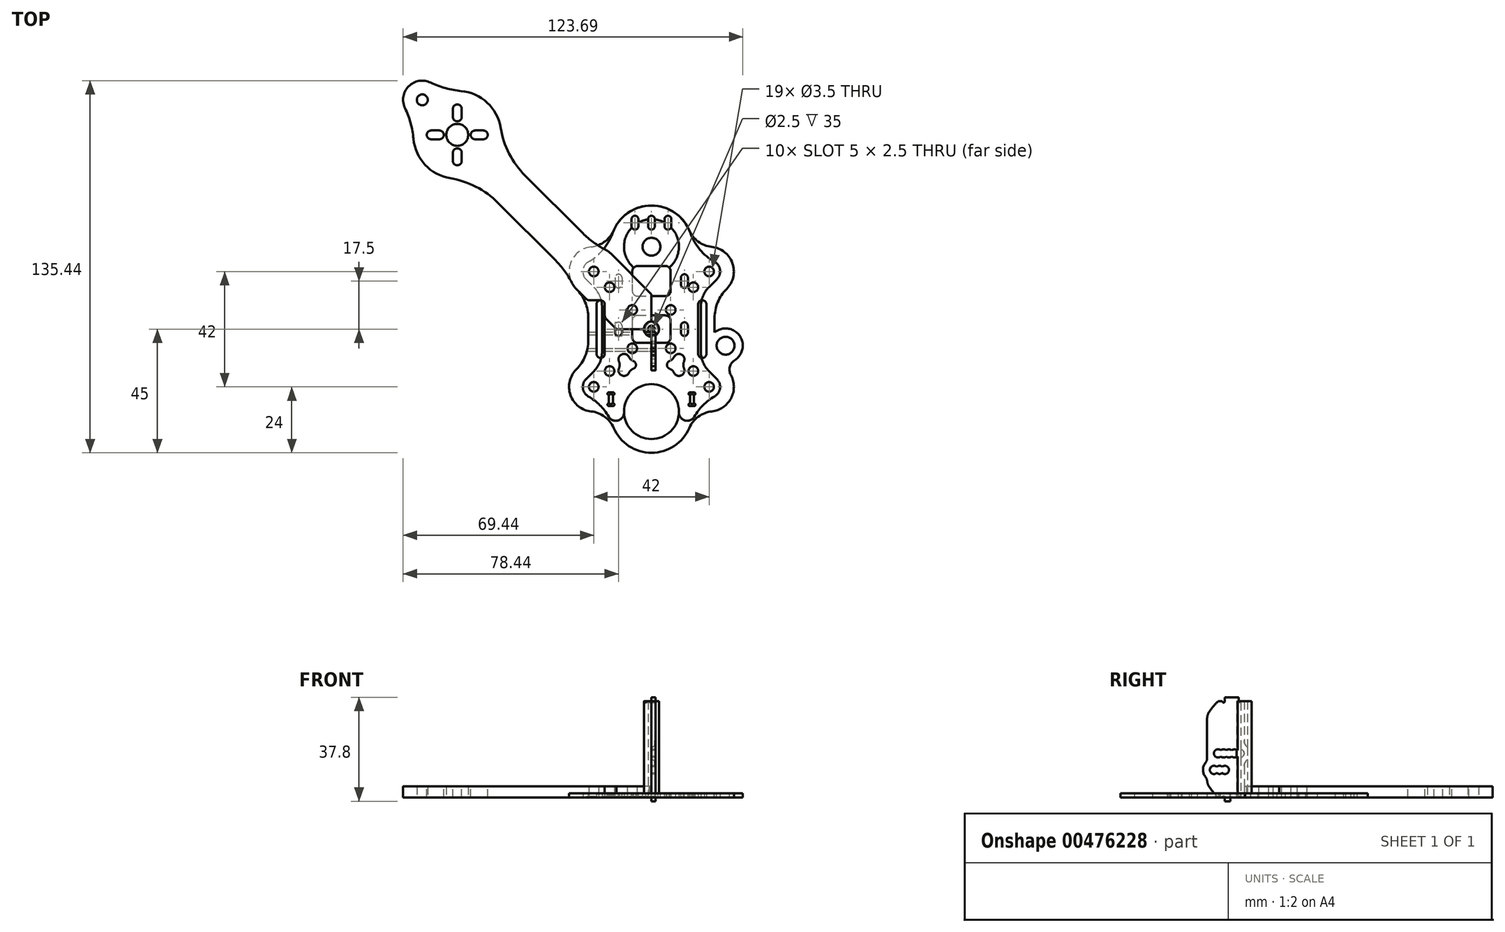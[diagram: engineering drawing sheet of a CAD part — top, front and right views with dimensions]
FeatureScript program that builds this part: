
annotation { "Feature Type Name" : "Feature", "Feature Type Description" : "" }
export const myFeature = defineFeature(function(context is Context, id is Id, definition is map)
    precondition{}
    {
        {
            var Q0;
            Q0=qCreatedBy(makeId("Top.planeOp"),FACE);
            var sketch = newSketch(context, id + "F0", { "sketchPlane" : qUnion([Q0])});
            skCircle(sketch, "E0", {"center": v(-15.25, 15.25) * mm, "radius": 1.75 * mm});
            skCircle(sketch, "E1", {"center": v(15.25, 15.25) * mm, "radius": 1.75 * mm});
            skCircle(sketch, "E2", {"center": v(15.25, -15.25) * mm, "radius": 1.75 * mm});
            skCircle(sketch, "E3", {"center": v(-15.25, -15.25) * mm, "radius": 1.75 * mm});
            skCircle(sketch, "E4", {"center": v(-7, 7) * mm, "radius": 1.75 * mm});
            skCircle(sketch, "E5.MirrorC", {"center": v(7, 7) * mm, "radius": 1.75 * mm});
            skCircle(sketch, "E6.MirrorC", {"center": v(-7, -7) * mm, "radius": 1.75 * mm});
            skCircle(sketch, "E7.MirrorC", {"center": v(7, -7) * mm, "radius": 1.75 * mm});
            skCircle(sketch, "E8", {"center": v(-21, 21) * mm, "radius": 1.75 * mm});
            skCircle(sketch, "E9.MirrorC", {"center": v(21, 21) * mm, "radius": 1.75 * mm});
            skCircle(sketch, "E10.MirrorC", {"center": v(-21, -21) * mm, "radius": 1.75 * mm});
            skCircle(sketch, "E11.MirrorC", {"center": v(21, -21) * mm, "radius": 1.75 * mm});
            skArc(sketch, "E12", {"start": v(-14.64, 27.36) * mm, "mid": v(-27.36, 27.36) * mm, "end": v(-27.36, 14.64) * mm});
            skLineSegment(sketch, "E13", {"start": v(-17, 9) * mm, "end": v(-17, -9.5) * mm});
            skLineSegment(sketch, "E14", {"start": v(-22.6, 10.5) * mm, "end": v(-18.5, 10.5) * mm});
            skLineSegment(sketch, "E15", {"start": v(-22.81, -10.5) * mm, "end": v(-18, -10.5) * mm});
            skLineSegment(sketch, "E16", {"start": v(-14.64, 27.36) * mm, "end": v(-12.37, 25.1) * mm});
            skLineSegment(sketch, "E17", {"start": v(-27.36, 14.64) * mm, "end": v(-23.67, 10.94) * mm});
            skLineSegment(sketch, "E18.MirrorCS", {"start": v(-27.36, -14.64) * mm, "end": v(-23.52, -10.8) * mm});
            skArc(sketch, "E19.MirrorCS", {"start": v(-14.64, -27.36) * mm, "mid": v(-27.36, -27.36) * mm, "end": v(-27.36, -14.64) * mm});
            skLineSegment(sketch, "E20.MirrorCS", {"start": v(-14.64, -27.36) * mm, "end": v(-12.37, -25.1) * mm});
            skLineSegment(sketch, "E21.MirrorCS", {"start": v(14.64, 27.36) * mm, "end": v(12.37, 25.1) * mm});
            skArc(sketch, "E22.MirrorCS", {"start": v(14.64, 27.36) * mm, "mid": v(27.36, 27.36) * mm, "end": v(27.36, 14.64) * mm});
            skLineSegment(sketch, "E23.MirrorCS", {"start": v(27.36, 14.64) * mm, "end": v(23.52, 10.8) * mm});
            skLineSegment(sketch, "E24.MirrorCS", {"start": v(22.81, 10.5) * mm, "end": v(18, 10.5) * mm});
            skLineSegment(sketch, "E25.MirrorCS", {"start": v(17, 9.5) * mm, "end": v(17, -9.5) * mm});
            skLineSegment(sketch, "E26.MirrorCS", {"start": v(22.81, -10.5) * mm, "end": v(18, -10.5) * mm});
            skLineSegment(sketch, "E27.MirrorCS", {"start": v(27.36, -14.64) * mm, "end": v(23.52, -10.8) * mm});
            skArc(sketch, "E28.MirrorCS", {"start": v(14.64, -27.36) * mm, "mid": v(27.36, -27.36) * mm, "end": v(27.36, -14.64) * mm});
            skLineSegment(sketch, "E29.MirrorCS", {"start": v(14.64, -27.36) * mm, "end": v(12.37, -25.1) * mm});
            skPoint(sketch, "E30.visualSharp", {"position": v(0, 12.73) * mm});
            skPoint(sketch, "E31.visualSharp", {"position": v(0, -12.73) * mm});
            skArc(sketch, "E31.filletArc", {"start": v(12.37, -25.1) * mm, "mid": v(0, -19.98) * mm, "end": v(-12.37, -25.1) * mm});
            skPoint(sketch, "E32.visualSharp", {"position": v(-23.23, 10.5) * mm});
            skArc(sketch, "E32.filletArc", {"start": v(-23.67, 10.94) * mm, "mid": v(-23.18, 10.61) * mm, "end": v(-22.6, 10.5) * mm});
            skPoint(sketch, "E33.visualSharp", {"position": v(-17, 10.5) * mm});
            skArc(sketch, "E33.filletArc", {"start": v(-17, 9) * mm, "mid": v(-17.44, 10.06) * mm, "end": v(-18.5, 10.5) * mm});
            skPoint(sketch, "E34.visualSharp", {"position": v(-17, -10.5) * mm});
            skArc(sketch, "E34.filletArc", {"start": v(-18, -10.5) * mm, "mid": v(-17.3, -10.2) * mm, "end": v(-17, -9.5) * mm});
            skPoint(sketch, "E35.visualSharp", {"position": v(-23.23, -10.5) * mm});
            skArc(sketch, "E35.filletArc", {"start": v(-22.81, -10.5) * mm, "mid": v(-23.2, -10.58) * mm, "end": v(-23.52, -10.8) * mm});
            skPoint(sketch, "E36.visualSharp", {"position": v(17, -10.5) * mm});
            skArc(sketch, "E36.filletArc", {"start": v(17, -9.5) * mm, "mid": v(17.3, -10.2) * mm, "end": v(18, -10.5) * mm});
            skPoint(sketch, "E37.visualSharp", {"position": v(23.23, -10.5) * mm});
            skArc(sketch, "E37.filletArc", {"start": v(23.52, -10.8) * mm, "mid": v(23.2, -10.58) * mm, "end": v(22.81, -10.5) * mm});
            skPoint(sketch, "E38.visualSharp", {"position": v(17, 10.5) * mm});
            skArc(sketch, "E38.filletArc", {"start": v(18, 10.5) * mm, "mid": v(17.3, 10.2) * mm, "end": v(17, 9.5) * mm});
            skPoint(sketch, "E39.visualSharp", {"position": v(23.23, 10.5) * mm});
            skArc(sketch, "E39.filletArc", {"start": v(22.81, 10.5) * mm, "mid": v(23.2, 10.58) * mm, "end": v(23.52, 10.8) * mm});
            skLineSegment(sketch, "E40", {"start": v(-21, 21) * mm, "end": v(0, 0) * mm, "construction": true});
            skArc(sketch, "E41.filletArc", {"start": v(-12.37, 25.1) * mm, "mid": v(0, 19.98) * mm, "end": v(12.37, 25.1) * mm});
            skSolve(sketch);
        }
        {
            var Q0;
            Q0=makeQuery(id+"F0.imprint","IMPRINT",FACE,{"disambiguationData":[TD([[makeQuery(id+"F0.imprint","IMPRINT",EDGE,{"derivedFrom":sQuery(id+"F0.wireOp",EDGE,"E0")}),-1.0]])]});
            extrude(context, id + "F1", {"entities" : qUnion([Q0]), "depth" : 1.5 * mm});
        }
        {
            var Q0;
            Q0=qCreatedBy(makeId("Top.planeOp"),FACE);
            var sketch = newSketch(context, id + "F2", { "sketchPlane" : qUnion([Q0])});
            skCircle(sketch, "E42", {"center": v(-15.25, 15.25) * mm, "radius": 1.75 * mm});
            skCircle(sketch, "E43", {"center": v(-7, 7) * mm, "radius": 2.23 * mm});
            skCircle(sketch, "E44", {"center": v(-21, 21) * mm, "radius": 1.75 * mm});
            skArc(sketch, "E45", {"start": v(-21.93, 29.95) * mm, "mid": v(-29.48, 24.01) * mm, "end": v(-27.36, 14.64) * mm});
            skLineSegment(sketch, "E46", {"start": v(-17, 9) * mm, "end": v(-17, 0) * mm});
            skLineSegment(sketch, "E47", {"start": v(-18.5, 10.5) * mm, "end": v(-18.5, 10.5) * mm});
            skLineSegment(sketch, "E48", {"start": v(-20, 9) * mm, "end": v(-20, 0) * mm});
            skPoint(sketch, "E49.visualSharp", {"position": v(-20, 10.5) * mm});
            skArc(sketch, "E49.filletArc", {"start": v(-18.5, 10.5) * mm, "mid": v(-19.56, 10.06) * mm, "end": v(-20, 9) * mm});
            skPoint(sketch, "E50.visualSharp", {"position": v(-17, 10.5) * mm});
            skArc(sketch, "E50.filletArc", {"start": v(-17, 9) * mm, "mid": v(-17.44, 10.06) * mm, "end": v(-18.5, 10.5) * mm});
            skArc(sketch, "E51", {"start": v(0, 45) * mm, "mid": v(-8.24, 42.53) * mm, "end": v(-13.77, 35.94) * mm});
            skArc(sketch, "E52", {"start": v(-21.93, 29.95) * mm, "mid": v(-17.04, 31.84) * mm, "end": v(-13.77, 35.94) * mm});
            skLineSegment(sketch, "E53", {"start": v(0, 45) * mm, "end": v(0, -45) * mm, "construction": true});
            skArc(sketch, "E54", {"start": v(0, 40) * mm, "mid": v(-10, 30) * mm, "end": v(0, 20) * mm});
            skArc(sketch, "E55.MirrorCS", {"start": v(18.5, 10.5) * mm, "mid": v(19.56, 10.06) * mm, "end": v(20, 9) * mm});
            skArc(sketch, "E56.MirrorCS", {"start": v(17, 9) * mm, "mid": v(17.44, 10.06) * mm, "end": v(18.5, 10.5) * mm});
            skLineSegment(sketch, "E57.MirrorCS", {"start": v(18.5, 10.5) * mm, "end": v(18.5, 10.5) * mm});
            skLineSegment(sketch, "E58.MirrorCS", {"start": v(17, 9) * mm, "end": v(17, 0) * mm});
            skArc(sketch, "E59.MirrorCS", {"start": v(21.93, 29.95) * mm, "mid": v(29.48, 24.01) * mm, "end": v(27.36, 14.64) * mm});
            skCircle(sketch, "E60.MirrorC", {"center": v(21, 21) * mm, "radius": 1.75 * mm});
            skCircle(sketch, "E61.MirrorC", {"center": v(7, 7) * mm, "radius": 2.23 * mm});
            skCircle(sketch, "E62.MirrorC", {"center": v(15.25, 15.25) * mm, "radius": 1.75 * mm});
            skArc(sketch, "E63.MirrorCS", {"start": v(21.93, 29.95) * mm, "mid": v(17.04, 31.84) * mm, "end": v(13.77, 35.94) * mm});
            skPoint(sketch, "E64.MirrorP", {"position": v(20, 10.5) * mm});
            skLineSegment(sketch, "E65.MirrorCS", {"start": v(20, 9) * mm, "end": v(20, 0) * mm});
            skPoint(sketch, "E66.MirrorP", {"position": v(17, 10.5) * mm});
            skArc(sketch, "E67.MirrorCS", {"start": v(0, 40) * mm, "mid": v(10, 30) * mm, "end": v(0, 20) * mm});
            skArc(sketch, "E68.MirrorCS", {"start": v(0, 45) * mm, "mid": v(8.24, 42.53) * mm, "end": v(13.77, 35.94) * mm});
            skPoint(sketch, "E69.MirrorP", {"position": v(20, -10.5) * mm});
            skLineSegment(sketch, "E70.MirrorCS", {"start": v(18.5, -10.5) * mm, "end": v(18.5, -10.5) * mm});
            skPoint(sketch, "E71.MirrorP", {"position": v(17, -10.5) * mm});
            skArc(sketch, "E72.MirrorCS", {"start": v(17, -9) * mm, "mid": v(17.44, -10.06) * mm, "end": v(18.5, -10.5) * mm});
            skLineSegment(sketch, "E73.MirrorCS", {"start": v(20, -9) * mm, "end": v(20, 0) * mm});
            skLineSegment(sketch, "E74.MirrorCS", {"start": v(17, -9) * mm, "end": v(17, 0) * mm});
            skArc(sketch, "E75.MirrorCS", {"start": v(18.5, -10.5) * mm, "mid": v(19.56, -10.06) * mm, "end": v(20, -9) * mm});
            skArc(sketch, "E76.MirrorCS", {"start": v(-17, -9) * mm, "mid": v(-17.44, -10.06) * mm, "end": v(-18.5, -10.5) * mm});
            skArc(sketch, "E77.MirrorCS", {"start": v(-18.5, -10.5) * mm, "mid": v(-19.56, -10.06) * mm, "end": v(-20, -9) * mm});
            skLineSegment(sketch, "E78.MirrorCS", {"start": v(-20, -9) * mm, "end": v(-20, 0) * mm});
            skLineSegment(sketch, "E79.MirrorCS", {"start": v(-17, -9) * mm, "end": v(-17, 0) * mm});
            skPoint(sketch, "E80.MirrorP", {"position": v(-20, -10.5) * mm});
            skPoint(sketch, "E81.MirrorP", {"position": v(-17, -10.5) * mm});
            skLineSegment(sketch, "E82.MirrorCS", {"start": v(-18.5, -10.5) * mm, "end": v(-18.5, -10.5) * mm});
            skCircle(sketch, "E83.MirrorC", {"center": v(-15.25, -15.25) * mm, "radius": 1.75 * mm});
            skCircle(sketch, "E84.MirrorC", {"center": v(-21, -21) * mm, "radius": 1.75 * mm});
            skArc(sketch, "E85.MirrorCS", {"start": v(-21.93, -29.95) * mm, "mid": v(-29.48, -24.01) * mm, "end": v(-27.36, -14.64) * mm});
            skCircle(sketch, "E86.MirrorC", {"center": v(21, -21) * mm, "radius": 1.75 * mm});
            skCircle(sketch, "E87.MirrorC", {"center": v(15.25, -15.25) * mm, "radius": 1.75 * mm});
            skCircle(sketch, "E88.MirrorC", {"center": v(7, -7) * mm, "radius": 2.23 * mm});
            skCircle(sketch, "E89.MirrorC", {"center": v(-7, -7) * mm, "radius": 2.23 * mm});
            skArc(sketch, "E90.MirrorCS", {"start": v(21.93, -29.95) * mm, "mid": v(29.48, -24.01) * mm, "end": v(27.36, -14.64) * mm});
            skArc(sketch, "E91.MirrorCS", {"start": v(21.93, -29.95) * mm, "mid": v(17.04, -31.84) * mm, "end": v(13.77, -35.94) * mm});
            skArc(sketch, "E92.MirrorCS", {"start": v(0, -45) * mm, "mid": v(8.24, -42.53) * mm, "end": v(13.77, -35.94) * mm});
            skArc(sketch, "E93.MirrorCS", {"start": v(0, -45) * mm, "mid": v(-8.24, -42.53) * mm, "end": v(-13.77, -35.94) * mm});
            skArc(sketch, "E94.MirrorCS", {"start": v(-21.93, -29.95) * mm, "mid": v(-17.04, -31.84) * mm, "end": v(-13.77, -35.94) * mm});
            skArc(sketch, "E95.MirrorCS", {"start": v(0, -40) * mm, "mid": v(-10, -30) * mm, "end": v(0, -20) * mm});
            skArc(sketch, "E96.MirrorCS", {"start": v(0, -40) * mm, "mid": v(10, -30) * mm, "end": v(0, -20) * mm});
            skLineSegment(sketch, "E97.bottom", {"start": v(-15.5, -23) * mm, "end": v(-14, -23) * mm});
            skLineSegment(sketch, "E97.top", {"start": v(-15.5, -28) * mm, "end": v(-14, -28) * mm});
            skLineSegment(sketch, "E97.left", {"start": v(-15.5, -23) * mm, "end": v(-15.5, -28) * mm});
            skLineSegment(sketch, "E97.right", {"start": v(-14, -23) * mm, "end": v(-14, -28) * mm});
            skLineSegment(sketch, "E98.MirrorCS", {"start": v(15.5, -23) * mm, "end": v(14, -23) * mm});
            skLineSegment(sketch, "E99.MirrorCS", {"start": v(15.5, -23) * mm, "end": v(15.5, -28) * mm});
            skLineSegment(sketch, "E100.MirrorCS", {"start": v(14, -23) * mm, "end": v(14, -28) * mm});
            skLineSegment(sketch, "E101.MirrorCS", {"start": v(15.5, -28) * mm, "end": v(14, -28) * mm});
            skLineSegment(sketch, "E102", {"start": v(-27.36, -14.64) * mm, "end": v(-27.36, -14.64) * mm});
            skLineSegment(sketch, "E103", {"start": v(-21, -21) * mm, "end": v(0, 0) * mm, "construction": true});
            skLineSegment(sketch, "E104", {"start": v(-22.97, -4.03) * mm, "end": v(-22.97, 0) * mm});
            skPoint(sketch, "E105.visualSharp", {"position": v(-22.97, -10.24) * mm});
            skArc(sketch, "E105.filletArc", {"start": v(-27.36, -14.64) * mm, "mid": v(-24.11, -9.77) * mm, "end": v(-22.97, -4.03) * mm});
            skArc(sketch, "E106.MirrorCS", {"start": v(27.36, -14.64) * mm, "mid": v(24.11, -9.77) * mm, "end": v(22.97, -4.03) * mm});
            skLineSegment(sketch, "E107.MirrorCS", {"start": v(22.97, -4.03) * mm, "end": v(22.97, 0) * mm});
            skArc(sketch, "E108.MirrorCS", {"start": v(27.36, 14.64) * mm, "mid": v(24.11, 9.77) * mm, "end": v(22.97, 4.03) * mm});
            skLineSegment(sketch, "E109.MirrorCS", {"start": v(22.97, 4.03) * mm, "end": v(22.97, 0) * mm});
            skLineSegment(sketch, "E110.MirrorCS", {"start": v(-22.97, 4.03) * mm, "end": v(-22.97, 0) * mm});
            skArc(sketch, "E111.MirrorCS", {"start": v(-27.36, 14.64) * mm, "mid": v(-24.11, 9.77) * mm, "end": v(-22.97, 4.03) * mm});
            skSolve(sketch);
        }
        {
            var Q0;
            Q0=makeQuery(id+"F2.imprint","IMPRINT",FACE,{"disambiguationData":[TD([[makeQuery(id+"F2.imprint","IMPRINT",EDGE,{"derivedFrom":sQuery(id+"F2.wireOp",EDGE,"E42")}),-1.0]])]});
            extrude(context, id + "F3", {"entities" : qUnion([Q0]), "depth" : 1.5 * mm});
        }
        {
            var Q0;
            Q0=makeQuery(id+"F3.opExtrude","CAP_FACE",FACE,{"disambiguationData":[OSD([sQuery(id+"F2.wireOp",EDGE,"E42"),sQuery(id+"F2.wireOp",EDGE,"E43"),sQuery(id+"F2.wireOp",EDGE,"E44"),sQuery(id+"F2.wireOp",EDGE,"E45"),sQuery(id+"F2.wireOp",EDGE,"E46"),sQuery(id+"F2.wireOp",EDGE,"E48"),sQuery(id+"F2.wireOp",EDGE,"E49.filletArc"),sQuery(id+"F2.wireOp",EDGE,"E50.filletArc"),sQuery(id+"F2.wireOp",EDGE,"E51"),sQuery(id+"F2.wireOp",EDGE,"E52"),sQuery(id+"F2.wireOp",EDGE,"E54"),sQuery(id+"F2.wireOp",EDGE,"E55.MirrorCS"),sQuery(id+"F2.wireOp",EDGE,"E56.MirrorCS"),sQuery(id+"F2.wireOp",EDGE,"E58.MirrorCS"),sQuery(id+"F2.wireOp",EDGE,"E59.MirrorCS"),sQuery(id+"F2.wireOp",EDGE,"E60.MirrorC"),sQuery(id+"F2.wireOp",EDGE,"E61.MirrorC"),sQuery(id+"F2.wireOp",EDGE,"E62.MirrorC"),sQuery(id+"F2.wireOp",EDGE,"E63.MirrorCS"),sQuery(id+"F2.wireOp",EDGE,"E65.MirrorCS"),sQuery(id+"F2.wireOp",EDGE,"E67.MirrorCS"),sQuery(id+"F2.wireOp",EDGE,"E68.MirrorCS"),sQuery(id+"F2.wireOp",EDGE,"E72.MirrorCS"),sQuery(id+"F2.wireOp",EDGE,"E73.MirrorCS"),sQuery(id+"F2.wireOp",EDGE,"E74.MirrorCS"),sQuery(id+"F2.wireOp",EDGE,"E75.MirrorCS"),sQuery(id+"F2.wireOp",EDGE,"E76.MirrorCS"),sQuery(id+"F2.wireOp",EDGE,"E77.MirrorCS"),sQuery(id+"F2.wireOp",EDGE,"E78.MirrorCS"),sQuery(id+"F2.wireOp",EDGE,"E79.MirrorCS"),sQuery(id+"F2.wireOp",EDGE,"E83.MirrorC"),sQuery(id+"F2.wireOp",EDGE,"E84.MirrorC"),sQuery(id+"F2.wireOp",EDGE,"E85.MirrorCS"),sQuery(id+"F2.wireOp",EDGE,"E86.MirrorC"),sQuery(id+"F2.wireOp",EDGE,"E87.MirrorC"),sQuery(id+"F2.wireOp",EDGE,"E88.MirrorC"),sQuery(id+"F2.wireOp",EDGE,"E89.MirrorC"),sQuery(id+"F2.wireOp",EDGE,"E90.MirrorCS"),sQuery(id+"F2.wireOp",EDGE,"E91.MirrorCS"),sQuery(id+"F2.wireOp",EDGE,"E92.MirrorCS"),sQuery(id+"F2.wireOp",EDGE,"E93.MirrorCS"),sQuery(id+"F2.wireOp",EDGE,"E94.MirrorCS"),sQuery(id+"F2.wireOp",EDGE,"E95.MirrorCS"),sQuery(id+"F2.wireOp",EDGE,"E96.MirrorCS"),sQuery(id+"F2.wireOp",EDGE,"E97.bottom"),sQuery(id+"F2.wireOp",EDGE,"E97.top"),sQuery(id+"F2.wireOp",EDGE,"E97.left"),sQuery(id+"F2.wireOp",EDGE,"E97.right"),sQuery(id+"F2.wireOp",EDGE,"E98.MirrorCS"),sQuery(id+"F2.wireOp",EDGE,"E99.MirrorCS"),sQuery(id+"F2.wireOp",EDGE,"E100.MirrorCS"),sQuery(id+"F2.wireOp",EDGE,"E101.MirrorCS"),sQuery(id+"F2.wireOp",EDGE,"E104"),sQuery(id+"F2.wireOp",EDGE,"E105.filletArc"),sQuery(id+"F2.wireOp",EDGE,"E106.MirrorCS"),sQuery(id+"F2.wireOp",EDGE,"E107.MirrorCS"),sQuery(id+"F2.wireOp",EDGE,"E108.MirrorCS"),sQuery(id+"F2.wireOp",EDGE,"E109.MirrorCS"),sQuery(id+"F2.wireOp",EDGE,"E110.MirrorCS"),sQuery(id+"F2.wireOp",EDGE,"E111.MirrorCS")])],"isStart":true});
            var sketch = newSketch(context, id + "F4", { "sketchPlane" : qUnion([Q0])});
            skCircle(sketch, "E112", {"center": v(-15.5, 27.5) * mm, "radius": 0.5 * mm});
            skCircle(sketch, "E113", {"center": v(-14, 27.5) * mm, "radius": 0.5 * mm});
            skCircle(sketch, "E114", {"center": v(-15.5, 23.5) * mm, "radius": 0.5 * mm});
            skCircle(sketch, "E115", {"center": v(-14, 23.5) * mm, "radius": 0.5 * mm});
            skCircle(sketch, "E116.MirrorC", {"center": v(14, 23.5) * mm, "radius": 0.5 * mm});
            skCircle(sketch, "E117.MirrorC", {"center": v(15.5, 27.5) * mm, "radius": 0.5 * mm});
            skCircle(sketch, "E118.MirrorC", {"center": v(14, 27.5) * mm, "radius": 0.5 * mm});
            skCircle(sketch, "E119.MirrorC", {"center": v(15.5, 23.5) * mm, "radius": 0.5 * mm});
            skSolve(sketch);
        }
        {
            var Q0;
            Q0 = qSketchRegion(id + "F4", true);
            extrude(context, id + "F5", {"entities" : qUnion([Q0]), "operationType" : NewBodyOperationType.REMOVE, "oppositeDirection" : true, "depth" : 25 * mm});
        }
        {
            var Q0;
            Q0=qCreatedBy(makeId("Top.planeOp"),FACE);
            var sketch = newSketch(context, id + "F6", { "sketchPlane" : qUnion([Q0])});
            skCircle(sketch, "E120", {"center": v(-7, 7) * mm, "radius": 1.75 * mm});
            skCircle(sketch, "E121", {"center": v(-15.25, 15.25) * mm, "radius": 1.75 * mm});
            skCircle(sketch, "E122", {"center": v(-21, 21) * mm, "radius": 1.75 * mm});
            skArc(sketch, "E123", {"start": v(-17, 9) * mm, "mid": v(-17.44, 10.06) * mm, "end": v(-18.5, 10.5) * mm});
            skLineSegment(sketch, "E124", {"start": v(0, 0) * mm, "end": v(-70.71, 70.71) * mm, "construction": true});
            skLineSegment(sketch, "E125", {"start": v(0, 12.73) * mm, "end": v(-14.64, 27.36) * mm});
            skLineSegment(sketch, "E126", {"start": v(-12.73, 0) * mm, "end": v(-16.56, 3.83) * mm});
            skLineSegment(sketch, "E127", {"start": v(-17, 9) * mm, "end": v(-17, 4.9) * mm});
            skLineSegment(sketch, "E128", {"start": v(-18.5, 10.5) * mm, "end": v(-22.6, 10.5) * mm});
            skLineSegment(sketch, "E129.trimOffspring", {"start": v(-23.67, 10.94) * mm, "end": v(-27.36, 14.64) * mm});
            skLineSegment(sketch, "E130", {"start": v(-12.73, 0) * mm, "end": v(0, 0) * mm});
            skLineSegment(sketch, "E131", {"start": v(0, 0) * mm, "end": v(0, 12.73) * mm});
            skPoint(sketch, "E132.visualSharp", {"position": v(-23.23, 10.5) * mm});
            skArc(sketch, "E132.filletArc", {"start": v(-23.67, 10.94) * mm, "mid": v(-23.18, 10.61) * mm, "end": v(-22.6, 10.5) * mm});
            skPoint(sketch, "E133.visualSharp", {"position": v(-17, 4.27) * mm});
            skArc(sketch, "E133.filletArc", {"start": v(-17, 4.9) * mm, "mid": v(-16.89, 4.32) * mm, "end": v(-16.56, 3.83) * mm});
            skArc(sketch, "E134", {"start": v(-86.65, 69.27) * mm, "mid": v(-82.43, 59.82) * mm, "end": v(-73.3, 54.92) * mm});
            skArc(sketch, "E135", {"start": v(-80.38, 89.73) * mm, "mid": v(-88.39, 88.39) * mm, "end": v(-89.73, 80.38) * mm});
            skCircle(sketch, "E136", {"center": v(-83.44, 83.44) * mm, "radius": 2 * mm});
            skLineSegment(sketch, "E137", {"start": v(-70.71, 70.71) * mm, "end": v(-83.44, 83.44) * mm, "construction": true});
            skPoint(sketch, "E138.visualSharp", {"position": v(-76.76, 85.52) * mm});
            skArc(sketch, "E138.filletArc", {"start": v(-80.38, 89.73) * mm, "mid": v(-74.97, 87.69) * mm, "end": v(-69.27, 86.65) * mm});
            skPoint(sketch, "E139.visualSharp", {"position": v(-85.52, 76.76) * mm});
            skArc(sketch, "E139.filletArc", {"start": v(-86.65, 69.27) * mm, "mid": v(-87.69, 74.97) * mm, "end": v(-89.73, 80.38) * mm});
            skCircle(sketch, "E140", {"center": v(-70.71, 70.71) * mm, "radius": 64.25 * mm, "construction": true});
            skArc(sketch, "E141.trimOffspring", {"start": v(-54.92, 73.3) * mm, "mid": v(-59.82, 82.43) * mm, "end": v(-69.27, 86.65) * mm});
            skCircle(sketch, "E142", {"center": v(-70.71, 70.71) * mm, "radius": 4 * mm});
            skArc(sketch, "E143.trimOffspring", {"start": v(-14.64, 27.36) * mm, "mid": v(-15.7, 28.28) * mm, "end": v(-16.9, 29.02) * mm});
            skLineSegment(sketch, "E144", {"start": v(-45.97, 55.87) * mm, "end": v(-25, 34.9) * mm});
            skLineSegment(sketch, "E145", {"start": v(-55.87, 45.97) * mm, "end": v(-34.9, 25) * mm});
            skPoint(sketch, "E146.visualSharp", {"position": v(-65.49, 55.59) * mm});
            skArc(sketch, "E146.filletArc", {"start": v(-55.87, 45.97) * mm, "mid": v(-63.89, 51.82) * mm, "end": v(-73.3, 54.92) * mm});
            skPoint(sketch, "E147.visualSharp", {"position": v(-55.59, 65.49) * mm});
            skArc(sketch, "E147.filletArc", {"start": v(-54.92, 73.3) * mm, "mid": v(-51.82, 63.89) * mm, "end": v(-45.97, 55.87) * mm});
            skArc(sketch, "E148.trimOffspring", {"start": v(-29.02, 16.9) * mm, "mid": v(-28.28, 15.7) * mm, "end": v(-27.36, 14.64) * mm});
            skPoint(sketch, "E149.visualSharp", {"position": v(-20.05, 29.95) * mm});
            skArc(sketch, "E149.filletArc", {"start": v(-25, 34.9) * mm, "mid": v(-21.18, 31.64) * mm, "end": v(-16.9, 29.02) * mm});
            skPoint(sketch, "E150.visualSharp", {"position": v(-29.95, 20.05) * mm});
            skArc(sketch, "E150.filletArc", {"start": v(-29.02, 16.9) * mm, "mid": v(-31.64, 21.18) * mm, "end": v(-34.9, 25) * mm});
            skSolve(sketch);
        }
        {
            var Q0;
            Q0=makeQuery(id+"F6.imprint","IMPRINT",FACE,{"disambiguationData":[TD([[makeQuery(id+"F6.imprint","IMPRINT",EDGE,{"derivedFrom":sQuery(id+"F6.wireOp",EDGE,"E120")}),-1.0]])]});
            extrude(context, id + "F7", {"entities" : qUnion([Q0]), "depth" : 4 * mm});
        }
        {
            var Q0;
            Q0=makeQuery(id+"F7.opExtrude","CAP_FACE",FACE,{"disambiguationData":[OSD([sQuery(id+"F6.wireOp",EDGE,"E120"),sQuery(id+"F6.wireOp",EDGE,"E121"),sQuery(id+"F6.wireOp",EDGE,"E122"),sQuery(id+"F6.wireOp",EDGE,"E123"),sQuery(id+"F6.wireOp",EDGE,"E125"),sQuery(id+"F6.wireOp",EDGE,"E126"),sQuery(id+"F6.wireOp",EDGE,"E127"),sQuery(id+"F6.wireOp",EDGE,"E128"),sQuery(id+"F6.wireOp",EDGE,"E129.trimOffspring"),sQuery(id+"F6.wireOp",EDGE,"E130"),sQuery(id+"F6.wireOp",EDGE,"E131"),sQuery(id+"F6.wireOp",EDGE,"E132.filletArc"),sQuery(id+"F6.wireOp",EDGE,"E133.filletArc"),sQuery(id+"F6.wireOp",EDGE,"E134"),sQuery(id+"F6.wireOp",EDGE,"E135"),sQuery(id+"F6.wireOp",EDGE,"E136"),sQuery(id+"F6.wireOp",EDGE,"E138.filletArc"),sQuery(id+"F6.wireOp",EDGE,"E139.filletArc"),sQuery(id+"F6.wireOp",EDGE,"E141.trimOffspring"),sQuery(id+"F6.wireOp",EDGE,"7c681801-0f79-4b64-9db9-c0788a7385f7.filletArc"),sQuery(id+"F6.wireOp",EDGE,"abeb74fd-95f9-49b4-a37d-9e8ca5098ea8.filletArc"),sQuery(id+"F6.wireOp",EDGE,"E142")])],"isStart":false});
            var sketch = newSketch(context, id + "F8", { "sketchPlane" : qUnion([Q0])});
            skLineSegment(sketch, "E151", {"start": v(-70.71, 70.71) * mm, "end": v(-64.21, 70.71) * mm, "construction": true});
            skLineSegment(sketch, "E152", {"start": v(-70.71, 70.71) * mm, "end": v(0, 0) * mm, "construction": true});
            skLineSegment(sketch, "E153", {"start": v(-64.21, 70.71) * mm, "end": v(-61.21, 70.71) * mm, "construction": true});
            skArc(sketch, "E154.0.startCap", {"start": v(-64.21, 69.11) * mm, "mid": v(-65.81, 70.71) * mm, "end": v(-64.21, 72.31) * mm});
            skArc(sketch, "E154.0.endCap", {"start": v(-61.21, 72.31) * mm, "mid": v(-59.61, 70.71) * mm, "end": v(-61.21, 69.11) * mm});
            skLineSegment(sketch, "E154.0.left", {"start": v(-64.21, 72.31) * mm, "end": v(-61.21, 72.31) * mm});
            skLineSegment(sketch, "E154.0.right", {"start": v(-64.21, 69.11) * mm, "end": v(-61.21, 69.11) * mm});
            skLineSegment(sketch, "E155.1.0", {"start": v(-72.31, 77.21) * mm, "end": v(-72.31, 80.21) * mm});
            skArc(sketch, "E155.1.1", {"start": v(-69.11, 77.21) * mm, "mid": v(-70.71, 75.61) * mm, "end": v(-72.31, 77.21) * mm});
            skLineSegment(sketch, "E155.1.2", {"start": v(-69.11, 77.21) * mm, "end": v(-69.11, 80.21) * mm});
            skArc(sketch, "E155.1.3", {"start": v(-72.31, 80.21) * mm, "mid": v(-70.71, 81.81) * mm, "end": v(-69.11, 80.21) * mm});
            skLineSegment(sketch, "E155.2.0", {"start": v(-77.21, 69.11) * mm, "end": v(-80.21, 69.11) * mm});
            skArc(sketch, "E155.2.1", {"start": v(-77.21, 72.31) * mm, "mid": v(-75.61, 70.71) * mm, "end": v(-77.21, 69.11) * mm});
            skLineSegment(sketch, "E155.2.2", {"start": v(-77.21, 72.31) * mm, "end": v(-80.21, 72.31) * mm});
            skArc(sketch, "E155.2.3", {"start": v(-80.21, 69.11) * mm, "mid": v(-81.81, 70.71) * mm, "end": v(-80.21, 72.31) * mm});
            skLineSegment(sketch, "E155.3.0", {"start": v(-69.11, 64.21) * mm, "end": v(-69.11, 61.21) * mm});
            skArc(sketch, "E155.3.1", {"start": v(-72.31, 64.21) * mm, "mid": v(-70.71, 65.81) * mm, "end": v(-69.11, 64.21) * mm});
            skLineSegment(sketch, "E155.3.2", {"start": v(-72.31, 64.21) * mm, "end": v(-72.31, 61.21) * mm});
            skArc(sketch, "E155.3.3", {"start": v(-69.11, 61.21) * mm, "mid": v(-70.71, 59.61) * mm, "end": v(-72.31, 61.21) * mm});
            skPoint(sketch, "E155.center", {"position": v(-70.71, 70.71) * mm});
            skSolve(sketch);
        }
        {
            var Q0;
            Q0 = qSketchRegion(id + "F8", true);
            extrude(context, id + "F9", {"entities" : qUnion([Q0]), "operationType" : NewBodyOperationType.REMOVE, "oppositeDirection" : true, "depth" : 25 * mm});
        }
        {
            var Q0;
            Q0=qCreatedBy(makeId("Top.planeOp"),FACE);
            var sketch = newSketch(context, id + "F10", { "sketchPlane" : qUnion([Q0])});
            skCircle(sketch, "E156", {"center": v(-21, 21) * mm, "radius": 1.75 * mm});
            skArc(sketch, "E157", {"start": v(-23, 24.47) * mm, "mid": v(-24.97, 21.53) * mm, "end": v(-23.83, 18.17) * mm});
            skArc(sketch, "E158", {"start": v(0, 45) * mm, "mid": v(-8.63, 42.27) * mm, "end": v(-14.12, 35.06) * mm});
            skArc(sketch, "E159", {"start": v(-23, 24.47) * mm, "mid": v(-17.61, 28.98) * mm, "end": v(-14.12, 35.06) * mm});
            skLineSegment(sketch, "E160", {"start": v(-23.83, 18.17) * mm, "end": v(-20.93, 15.27) * mm});
            skLineSegment(sketch, "E161", {"start": v(-21, 21) * mm, "end": v(0, 0) * mm, "construction": true});
            skLineSegment(sketch, "E162", {"start": v(-18, 8.2) * mm, "end": v(-18, 0) * mm});
            skPoint(sketch, "E163.visualSharp", {"position": v(-18, 12.34) * mm});
            skArc(sketch, "E163.filletArc", {"start": v(-18, 8.2) * mm, "mid": v(-18.76, 12.03) * mm, "end": v(-20.93, 15.27) * mm});
            skLineSegment(sketch, "E164", {"start": v(0, 0) * mm, "end": v(0, 0) * mm});
            skLineSegment(sketch, "E165.MirrorCS", {"start": v(18, 8.2) * mm, "end": v(18, 0) * mm});
            skPoint(sketch, "E166.MirrorP", {"position": v(18, 12.34) * mm});
            skArc(sketch, "E167.MirrorCS", {"start": v(23, 24.47) * mm, "mid": v(17.61, 28.98) * mm, "end": v(14.12, 35.06) * mm});
            skLineSegment(sketch, "E168.MirrorCS", {"start": v(23.83, 18.17) * mm, "end": v(20.93, 15.27) * mm});
            skArc(sketch, "E169.MirrorCS", {"start": v(23, 24.47) * mm, "mid": v(24.97, 21.53) * mm, "end": v(23.83, 18.17) * mm});
            skCircle(sketch, "E170.MirrorC", {"center": v(21, 21) * mm, "radius": 1.75 * mm});
            skArc(sketch, "E171.MirrorCS", {"start": v(0, 45) * mm, "mid": v(8.63, 42.27) * mm, "end": v(14.12, 35.06) * mm});
            skLineSegment(sketch, "E172.MirrorCS", {"start": v(21, 21) * mm, "end": v(0, 0) * mm, "construction": true});
            skArc(sketch, "E173.MirrorCS", {"start": v(18, 8.2) * mm, "mid": v(18.76, 12.03) * mm, "end": v(20.93, 15.27) * mm});
            skLineSegment(sketch, "E174.MirrorCS", {"start": v(0, 45) * mm, "end": v(0, 0) * mm, "construction": true});
            skArc(sketch, "E175.MirrorCS", {"start": v(-18, -8.2) * mm, "mid": v(-18.76, -12.03) * mm, "end": v(-20.93, -15.27) * mm});
            skLineSegment(sketch, "E176.MirrorCS", {"start": v(-18, -8.2) * mm, "end": v(-18, 0) * mm});
            skLineSegment(sketch, "E177.MirrorCS", {"start": v(18, -8.2) * mm, "end": v(18, 0) * mm});
            skArc(sketch, "E178.MirrorCS", {"start": v(18, -8.2) * mm, "mid": v(18.76, -12.03) * mm, "end": v(20.93, -15.27) * mm});
            skLineSegment(sketch, "E179.MirrorCS", {"start": v(23.83, -18.17) * mm, "end": v(20.93, -15.27) * mm});
            skLineSegment(sketch, "E180.MirrorCS", {"start": v(-23.83, -18.17) * mm, "end": v(-20.93, -15.27) * mm});
            skArc(sketch, "E181.MirrorCS", {"start": v(-23, -24.47) * mm, "mid": v(-24.97, -21.53) * mm, "end": v(-23.83, -18.17) * mm});
            skArc(sketch, "E182.MirrorCS", {"start": v(23, -24.47) * mm, "mid": v(24.97, -21.53) * mm, "end": v(23.83, -18.17) * mm});
            skArc(sketch, "E183.MirrorCS", {"start": v(23, -24.47) * mm, "mid": v(18.8, -27.67) * mm, "end": v(15.6, -31.86) * mm});
            skArc(sketch, "E184.MirrorCS", {"start": v(-23, -24.47) * mm, "mid": v(-18.8, -27.67) * mm, "end": v(-15.6, -31.86) * mm});
            skCircle(sketch, "E185.MirrorC", {"center": v(-21, -21) * mm, "radius": 1.75 * mm});
            skCircle(sketch, "E186.MirrorC", {"center": v(21, -21) * mm, "radius": 1.75 * mm});
            skArc(sketch, "E187", {"start": v(10, -30) * mm, "mid": v(0, -20) * mm, "end": v(-10, -30) * mm});
            skLineSegment(sketch, "E188", {"start": v(-10, -30) * mm, "end": v(-10, -30.36) * mm});
            skLineSegment(sketch, "E189.MirrorCS", {"start": v(10, -30) * mm, "end": v(10, -30.36) * mm});
            skPoint(sketch, "E190.orphan", {"position": v(0, -45) * mm});
            skArc(sketch, "E191", {"start": v(-15.6, -31.86) * mm, "mid": v(-12.23, -33.26) * mm, "end": v(-10, -30.36) * mm});
            skPoint(sketch, "E192.orphan", {"position": v(-14.12, -35.06) * mm});
            skArc(sketch, "E193.MirrorCS", {"start": v(15.6, -31.86) * mm, "mid": v(12.23, -33.26) * mm, "end": v(10, -30.36) * mm});
            skPoint(sketch, "E194.orphan", {"position": v(14.12, -35.06) * mm});
            skLineSegment(sketch, "E195.bottom", {"start": v(-15.5, -23) * mm, "end": v(-14, -23) * mm});
            skLineSegment(sketch, "E195.top", {"start": v(-15.5, -28) * mm, "end": v(-14, -28) * mm});
            skLineSegment(sketch, "E195.left", {"start": v(-15.5, -23) * mm, "end": v(-15.5, -28) * mm});
            skLineSegment(sketch, "E195.right", {"start": v(-14, -23) * mm, "end": v(-14, -28) * mm});
            skLineSegment(sketch, "E196.MirrorCS", {"start": v(15.5, -28) * mm, "end": v(14, -28) * mm});
            skLineSegment(sketch, "E197.MirrorCS", {"start": v(14, -23) * mm, "end": v(14, -28) * mm});
            skLineSegment(sketch, "E198.MirrorCS", {"start": v(15.5, -23) * mm, "end": v(15.5, -28) * mm});
            skLineSegment(sketch, "E199.MirrorCS", {"start": v(15.5, -23) * mm, "end": v(14, -23) * mm});
            skSolve(sketch);
        }
        {
            var Q0;
            Q0=makeQuery(id+"F10.imprint","IMPRINT",FACE,{"disambiguationData":[TD([[makeQuery(id+"F10.imprint","IMPRINT",EDGE,{"derivedFrom":sQuery(id+"F10.wireOp",EDGE,"E156")}),-1.0]])]});
            extrude(context, id + "F11", {"entities" : qUnion([Q0]), "depth" : 1.5 * mm});
        }
        {
            var Q0;
            Q0=makeQuery(id+"F11.opExtrude","CAP_FACE",FACE,{"disambiguationData":[OSD([sQuery(id+"F10.wireOp",EDGE,"E156"),sQuery(id+"F10.wireOp",EDGE,"E157"),sQuery(id+"F10.wireOp",EDGE,"E158"),sQuery(id+"F10.wireOp",EDGE,"E159"),sQuery(id+"F10.wireOp",EDGE,"E160"),sQuery(id+"F10.wireOp",EDGE,"E162"),sQuery(id+"F10.wireOp",EDGE,"E163.filletArc"),sQuery(id+"F10.wireOp",EDGE,"E165.MirrorCS"),sQuery(id+"F10.wireOp",EDGE,"E167.MirrorCS"),sQuery(id+"F10.wireOp",EDGE,"E168.MirrorCS"),sQuery(id+"F10.wireOp",EDGE,"E169.MirrorCS"),sQuery(id+"F10.wireOp",EDGE,"E170.MirrorC"),sQuery(id+"F10.wireOp",EDGE,"E171.MirrorCS"),sQuery(id+"F10.wireOp",EDGE,"E173.MirrorCS"),sQuery(id+"F10.wireOp",EDGE,"E175.MirrorCS"),sQuery(id+"F10.wireOp",EDGE,"E176.MirrorCS"),sQuery(id+"F10.wireOp",EDGE,"E177.MirrorCS"),sQuery(id+"F10.wireOp",EDGE,"E178.MirrorCS"),sQuery(id+"F10.wireOp",EDGE,"E179.MirrorCS"),sQuery(id+"F10.wireOp",EDGE,"E180.MirrorCS"),sQuery(id+"F10.wireOp",EDGE,"E181.MirrorCS"),sQuery(id+"F10.wireOp",EDGE,"E182.MirrorCS"),sQuery(id+"F10.wireOp",EDGE,"E183.MirrorCS"),sQuery(id+"F10.wireOp",EDGE,"E184.MirrorCS"),sQuery(id+"F10.wireOp",EDGE,"E185.MirrorC"),sQuery(id+"F10.wireOp",EDGE,"E186.MirrorC"),sQuery(id+"F10.wireOp",EDGE,"E187"),sQuery(id+"F10.wireOp",EDGE,"E188"),sQuery(id+"F10.wireOp",EDGE,"E189.MirrorCS"),sQuery(id+"F10.wireOp",EDGE,"E191"),sQuery(id+"F10.wireOp",EDGE,"E193.MirrorCS"),sQuery(id+"F10.wireOp",EDGE,"E195.bottom"),sQuery(id+"F10.wireOp",EDGE,"E195.top"),sQuery(id+"F10.wireOp",EDGE,"E195.left"),sQuery(id+"F10.wireOp",EDGE,"E195.right"),sQuery(id+"F10.wireOp",EDGE,"E196.MirrorCS"),sQuery(id+"F10.wireOp",EDGE,"E197.MirrorCS"),sQuery(id+"F10.wireOp",EDGE,"E198.MirrorCS"),sQuery(id+"F10.wireOp",EDGE,"E199.MirrorCS")])],"isStart":false});
            var sketch = newSketch(context, id + "F12", { "sketchPlane" : qUnion([Q0])});
            skCircle(sketch, "E200", {"center": v(-14, -23.5) * mm, "radius": 0.5 * mm});
            skCircle(sketch, "E201", {"center": v(-15.5, -23.5) * mm, "radius": 0.5 * mm});
            skCircle(sketch, "E202", {"center": v(-15.5, -27.5) * mm, "radius": 0.5 * mm});
            skCircle(sketch, "E203", {"center": v(-14, -27.5) * mm, "radius": 0.5 * mm});
            skCircle(sketch, "E204.MirrorC", {"center": v(14, -27.5) * mm, "radius": 0.5 * mm});
            skCircle(sketch, "E205.MirrorC", {"center": v(15.5, -27.5) * mm, "radius": 0.5 * mm});
            skCircle(sketch, "E206.MirrorC", {"center": v(15.5, -23.5) * mm, "radius": 0.5 * mm});
            skCircle(sketch, "E207.MirrorC", {"center": v(14, -23.5) * mm, "radius": 0.5 * mm});
            skSolve(sketch);
        }
        {
            var Q0;
            Q0 = qSketchRegion(id + "F12", true);
            extrude(context, id + "F13", {"entities" : qUnion([Q0]), "operationType" : NewBodyOperationType.REMOVE, "oppositeDirection" : true, "depth" : 25 * mm});
        }
        {
            var Q0;
            Q0=qCreatedBy(makeId("Right.planeOp"),FACE);
            var sketch = newSketch(context, id + "F14", { "sketchPlane" : qUnion([Q0])});
            skLineSegment(sketch, "E208.bottom", {"start": v(-2, 35) * mm, "end": v(0, 35) * mm});
            skLineSegment(sketch, "E208.top", {"start": v(-2, 0) * mm, "end": v(0, 0) * mm});
            skLineSegment(sketch, "E208.left", {"start": v(0, 35) * mm, "end": v(0, 20.7) * mm});
            skArc(sketch, "E209", {"start": v(-2.5, 14.88) * mm, "mid": v(0, 16) * mm, "end": v(-2.5, 17.12) * mm});
            skArc(sketch, "E210.1.0.0", {"start": v(-4.5, 14.88) * mm, "mid": v(-3.5, 14.5) * mm, "end": v(-2.5, 14.88) * mm});
            skArc(sketch, "E210.2.0.0", {"start": v(-6.5, 14.88) * mm, "mid": v(-5.5, 14.5) * mm, "end": v(-4.5, 14.88) * mm});
            skArc(sketch, "E210.3.0.0", {"start": v(-8.5, 14.88) * mm, "mid": v(-7.5, 14.5) * mm, "end": v(-6.5, 14.88) * mm});
            skArc(sketch, "E210.4.0.0", {"start": v(-11, 16) * mm, "mid": v(-10.11, 14.63) * mm, "end": v(-8.5, 14.88) * mm});
            skLineSegment(sketch, "E210.direction1", {"start": v(-1.5, 16) * mm, "end": v(-3.5, 16) * mm, "construction": true});
            skArc(sketch, "E211.trimOffspring", {"start": v(-8.5, 17.12) * mm, "mid": v(-10.11, 17.37) * mm, "end": v(-11, 16) * mm});
            skArc(sketch, "E212.trimOffspring", {"start": v(-6.5, 17.12) * mm, "mid": v(-7.5, 17.5) * mm, "end": v(-8.5, 17.12) * mm});
            skArc(sketch, "E213.trimOffspring", {"start": v(-4.5, 17.12) * mm, "mid": v(-5.5, 17.5) * mm, "end": v(-6.5, 17.12) * mm});
            skArc(sketch, "E214.trimOffspring", {"start": v(-2.5, 17.12) * mm, "mid": v(-3.5, 17.5) * mm, "end": v(-4.5, 17.12) * mm});
            skLineSegment(sketch, "E215.top", {"start": v(-7, 36.4) * mm, "end": v(-2, 36.4) * mm});
            skLineSegment(sketch, "E215.left", {"start": v(-7, 35) * mm, "end": v(-7, 36.4) * mm});
            skLineSegment(sketch, "E215.right", {"start": v(-2, 35) * mm, "end": v(-2, 36.4) * mm});
            skLineSegment(sketch, "E216.trimOffspring", {"start": v(-9.42, 35) * mm, "end": v(-7, 35) * mm});
            skLineSegment(sketch, "E217.top", {"start": v(-2, -1.4) * mm, "end": v(-7, -1.4) * mm});
            skLineSegment(sketch, "E217.left", {"start": v(-2, 0) * mm, "end": v(-2, -1.4) * mm});
            skLineSegment(sketch, "E217.right", {"start": v(-7, 0) * mm, "end": v(-7, -1.4) * mm});
            skLineSegment(sketch, "E218.trimOffspring", {"start": v(-9.42, 0) * mm, "end": v(-7, 0) * mm});
            skLineSegment(sketch, "E219.trimOffspring", {"start": v(0, 11.3) * mm, "end": v(0, 0) * mm});
            skArc(sketch, "E220", {"start": v(0.92, 13.47) * mm, "mid": v(2, 16) * mm, "end": v(0.92, 18.53) * mm});
            skPoint(sketch, "E221.visualSharp", {"position": v(0, 12.84) * mm});
            skArc(sketch, "E221.filletArc", {"start": v(0.92, 13.47) * mm, "mid": v(0.24, 12.49) * mm, "end": v(0, 11.3) * mm});
            skPoint(sketch, "E222.visualSharp", {"position": v(0, 19.16) * mm});
            skArc(sketch, "E222.filletArc", {"start": v(0, 20.7) * mm, "mid": v(0.24, 19.51) * mm, "end": v(0.92, 18.53) * mm});
            skArc(sketch, "E223", {"start": v(-9.42, 35) * mm, "mid": v(-11.1, 33.27) * mm, "end": v(-12.58, 31.38) * mm});
            skPoint(sketch, "E223.centerSnap0", {"position": v(2, 16) * mm});
            skLineSegment(sketch, "E224", {"start": v(-13.5, 28.49) * mm, "end": v(-13.5, 13.12) * mm});
            skArc(sketch, "E225.trimOffspring", {"start": v(-12.58, 3.62) * mm, "mid": v(-11.1, 1.73) * mm, "end": v(-9.42, 0) * mm});
            skPoint(sketch, "E226.visualSharp", {"position": v(-13.5, 29.98) * mm});
            skArc(sketch, "E226.filletArc", {"start": v(-12.58, 31.38) * mm, "mid": v(-13.26, 30) * mm, "end": v(-13.5, 28.49) * mm});
            skPoint(sketch, "E227.visualSharp", {"position": v(-13.5, 5.02) * mm});
            skArc(sketch, "E227.filletArc", {"start": v(-13.5, 6.51) * mm, "mid": v(-13.26, 5) * mm, "end": v(-12.58, 3.62) * mm});
            skArc(sketch, "E228", {"start": v(-10, 11.12) * mm, "mid": v(-12.5, 10) * mm, "end": v(-10, 8.88) * mm});
            skArc(sketch, "E229", {"start": v(-13.5, 13.12) * mm, "mid": v(-15, 10) * mm, "end": v(-13.5, 6.88) * mm});
            skLineSegment(sketch, "E230.trimOffspring", {"start": v(-13.5, 6.88) * mm, "end": v(-13.5, 6.51) * mm});
            skArc(sketch, "E231.1.0.0", {"start": v(-10, 8.88) * mm, "mid": v(-9, 8.5) * mm, "end": v(-8, 8.88) * mm});
            skArc(sketch, "E231.2.0.0", {"start": v(-8, 8.88) * mm, "mid": v(-5.5, 10) * mm, "end": v(-8, 11.12) * mm});
            skLineSegment(sketch, "E231.direction1", {"start": v(-11, 10) * mm, "end": v(-9, 10) * mm, "construction": true});
            skArc(sketch, "E232.trimOffspring", {"start": v(-8, 11.12) * mm, "mid": v(-9, 11.5) * mm, "end": v(-10, 11.12) * mm});
            skSolve(sketch);
        }
        {
            var Q0;
            Q0=makeQuery(id+"F14.imprint","IMPRINT",FACE,{"disambiguationData":[TD([[makeQuery(id+"F14.imprint","IMPRINT",EDGE,{"derivedFrom":sQuery(id+"F14.wireOp",EDGE,"E208.bottom")}),-1.0]])]});
            extrude(context, id + "F15", {"entities" : qUnion([Q0]), "depth" : 1.5 * mm});
        }
        {
            var Q0;
            Q0=qCreatedBy(makeId("Top.planeOp"),FACE);
            var sketch = newSketch(context, id + "F16", { "sketchPlane" : qUnion([Q0])});
            skCircle(sketch, "E233", {"center": v(0, 0) * mm, "radius": 2.75 * mm});
            skCircle(sketch, "E234", {"center": v(0, 0) * mm, "radius": 1.25 * mm});
            skSolve(sketch);
        }
        {
            var Q0;
            Q0=makeQuery(id+"F16.imprint","IMPRINT",FACE,{"disambiguationData":[TD([[makeQuery(id+"F16.imprint","IMPRINT",EDGE,{"derivedFrom":sQuery(id+"F16.wireOp",EDGE,"E233")}),1.0]])]});
            extrude(context, id + "F17", {"entities" : qUnion([Q0]), "depth" : 35 * mm});
        }
        {
            var Q0;
            Q0=makeQuery(id+"F15.opExtrude","CAP_FACE",FACE,{"disambiguationData":[OSD([sQuery(id+"F14.wireOp",EDGE,"E208.bottom"),sQuery(id+"F14.wireOp",EDGE,"E208.top"),sQuery(id+"F14.wireOp",EDGE,"E208.left"),sQuery(id+"F14.wireOp",EDGE,"E209"),sQuery(id+"F14.wireOp",EDGE,"E210.1.0.0"),sQuery(id+"F14.wireOp",EDGE,"E210.2.0.0"),sQuery(id+"F14.wireOp",EDGE,"E210.3.0.0"),sQuery(id+"F14.wireOp",EDGE,"E210.4.0.0"),sQuery(id+"F14.wireOp",EDGE,"E210.5.0.0"),sQuery(id+"F14.wireOp",EDGE,"xB9VpMqL-v4Ol-apgo-nwYP-rYTZXYth8aNc"),sQuery(id+"F14.wireOp",EDGE,"E211.trimOffspring"),sQuery(id+"F14.wireOp",EDGE,"E212.trimOffspring"),sQuery(id+"F14.wireOp",EDGE,"E213.trimOffspring"),sQuery(id+"F14.wireOp",EDGE,"E214.trimOffspring"),sQuery(id+"F14.wireOp",EDGE,"E215.top"),sQuery(id+"F14.wireOp",EDGE,"E215.left"),sQuery(id+"F14.wireOp",EDGE,"E215.right"),sQuery(id+"F14.wireOp",EDGE,"E216.trimOffspring"),sQuery(id+"F14.wireOp",EDGE,"E217.top"),sQuery(id+"F14.wireOp",EDGE,"E217.left"),sQuery(id+"F14.wireOp",EDGE,"E217.right"),sQuery(id+"F14.wireOp",EDGE,"E218.trimOffspring"),sQuery(id+"F14.wireOp",EDGE,"WIyuLMze-qAqz-E62j-FoWG-WqTvR0OcbL3D"),sQuery(id+"F14.wireOp",EDGE,"idC8aPui-4hui-ehFC-vCG2-AV8bdVe3rIMw"),sQuery(id+"F14.wireOp",EDGE,"ff45fd1d-5618-4143-a879-ec99c5352242.trimOffspring"),sQuery(id+"F14.wireOp",EDGE,"E219.trimOffspring"),sQuery(id+"F14.wireOp",EDGE,"1a2c7717-6830-44b7-88a1-cf8e776470c7.filletArc"),sQuery(id+"F14.wireOp",EDGE,"16ee3bd6-ff6a-4e26-9a1d-72609509d275.filletArc"),sQuery(id+"F14.wireOp",EDGE,"2e36fd83-ecfd-4026-90d2-29abf45e5091.filletArc"),sQuery(id+"F14.wireOp",EDGE,"4da7e552-ee41-47cd-9aed-4835db0d361f.filletArc")])],"isStart":false});
            var sketch = newSketch(context, id + "F18", { "sketchPlane" : qUnion([Q0])});
            skCircle(sketch, "E235", {"center": v(-7.5, 35) * mm, "radius": 0.5 * mm});
            skCircle(sketch, "E236", {"center": v(-1.5, 35) * mm, "radius": 0.5 * mm});
            skCircle(sketch, "E237", {"center": v(-7.5, 0) * mm, "radius": 0.5 * mm});
            skCircle(sketch, "E238", {"center": v(-1.5, 0) * mm, "radius": 0.5 * mm});
            skSolve(sketch);
        }
        {
            var Q0;
            Q0 = qSketchRegion(id + "F18", true);
            extrude(context, id + "F19", {"entities" : qUnion([Q0]), "operationType" : NewBodyOperationType.REMOVE, "oppositeDirection" : true, "depth" : 25 * mm});
        }
        {
            var Q0;
            Q0=makeQuery(id+"F11.opExtrude","CAP_FACE",FACE,{"disambiguationData":[OSD([sQuery(id+"F10.wireOp",EDGE,"E156"),sQuery(id+"F10.wireOp",EDGE,"E157"),sQuery(id+"F10.wireOp",EDGE,"E158"),sQuery(id+"F10.wireOp",EDGE,"E159"),sQuery(id+"F10.wireOp",EDGE,"E160"),sQuery(id+"F10.wireOp",EDGE,"E162"),sQuery(id+"F10.wireOp",EDGE,"E163.filletArc"),sQuery(id+"F10.wireOp",EDGE,"E165.MirrorCS"),sQuery(id+"F10.wireOp",EDGE,"E167.MirrorCS"),sQuery(id+"F10.wireOp",EDGE,"E168.MirrorCS"),sQuery(id+"F10.wireOp",EDGE,"E169.MirrorCS"),sQuery(id+"F10.wireOp",EDGE,"E170.MirrorC"),sQuery(id+"F10.wireOp",EDGE,"E171.MirrorCS"),sQuery(id+"F10.wireOp",EDGE,"E173.MirrorCS"),sQuery(id+"F10.wireOp",EDGE,"E175.MirrorCS"),sQuery(id+"F10.wireOp",EDGE,"E176.MirrorCS"),sQuery(id+"F10.wireOp",EDGE,"E177.MirrorCS"),sQuery(id+"F10.wireOp",EDGE,"E178.MirrorCS"),sQuery(id+"F10.wireOp",EDGE,"E179.MirrorCS"),sQuery(id+"F10.wireOp",EDGE,"E180.MirrorCS"),sQuery(id+"F10.wireOp",EDGE,"E181.MirrorCS"),sQuery(id+"F10.wireOp",EDGE,"E182.MirrorCS"),sQuery(id+"F10.wireOp",EDGE,"E183.MirrorCS"),sQuery(id+"F10.wireOp",EDGE,"E184.MirrorCS"),sQuery(id+"F10.wireOp",EDGE,"E185.MirrorC"),sQuery(id+"F10.wireOp",EDGE,"E186.MirrorC"),sQuery(id+"F10.wireOp",EDGE,"E187"),sQuery(id+"F10.wireOp",EDGE,"E188"),sQuery(id+"F10.wireOp",EDGE,"E189.MirrorCS"),sQuery(id+"F10.wireOp",EDGE,"E191"),sQuery(id+"F10.wireOp",EDGE,"E193.MirrorCS"),sQuery(id+"F10.wireOp",EDGE,"E195.bottom"),sQuery(id+"F10.wireOp",EDGE,"E195.top"),sQuery(id+"F10.wireOp",EDGE,"E195.left"),sQuery(id+"F10.wireOp",EDGE,"E195.right"),sQuery(id+"F10.wireOp",EDGE,"E196.MirrorCS"),sQuery(id+"F10.wireOp",EDGE,"E197.MirrorCS"),sQuery(id+"F10.wireOp",EDGE,"E198.MirrorCS"),sQuery(id+"F10.wireOp",EDGE,"E199.MirrorCS")])],"isStart":false});
            var sketch = newSketch(context, id + "F20", { "sketchPlane" : qUnion([Q0])});
            skLineSegment(sketch, "E239", {"start": v(0, 40) * mm, "end": v(0, 37.5) * mm, "construction": true});
            skLineSegment(sketch, "E240", {"start": v(-6, 40) * mm, "end": v(-6, 37.5) * mm, "construction": true});
            skArc(sketch, "E241.0.startCap", {"start": v(-7.25, 40) * mm, "mid": v(-6, 41.25) * mm, "end": v(-4.75, 40) * mm});
            skArc(sketch, "E241.0.endCap", {"start": v(-4.75, 37.5) * mm, "mid": v(-6, 36.25) * mm, "end": v(-7.25, 37.5) * mm});
            skLineSegment(sketch, "E241.0.left", {"start": v(-4.75, 40) * mm, "end": v(-4.75, 37.5) * mm});
            skLineSegment(sketch, "E241.0.right", {"start": v(-7.25, 40) * mm, "end": v(-7.25, 37.5) * mm});
            skArc(sketch, "E242.0.startCap", {"start": v(-1.25, 40) * mm, "mid": v(0, 41.25) * mm, "end": v(1.25, 40) * mm});
            skArc(sketch, "E242.0.endCap", {"start": v(1.25, 37.5) * mm, "mid": v(0, 36.25) * mm, "end": v(-1.25, 37.5) * mm});
            skLineSegment(sketch, "E242.0.left", {"start": v(1.25, 40) * mm, "end": v(1.25, 37.5) * mm});
            skLineSegment(sketch, "E242.0.right", {"start": v(-1.25, 40) * mm, "end": v(-1.25, 37.5) * mm});
            skLineSegment(sketch, "E243.MirrorCS", {"start": v(7.25, 40) * mm, "end": v(7.25, 37.5) * mm});
            skLineSegment(sketch, "E244.MirrorCS", {"start": v(4.75, 40) * mm, "end": v(4.75, 37.5) * mm});
            skArc(sketch, "E245.MirrorCS", {"start": v(4.75, 37.5) * mm, "mid": v(6, 36.25) * mm, "end": v(7.25, 37.5) * mm});
            skArc(sketch, "E246.MirrorCS", {"start": v(7.25, 40) * mm, "mid": v(6, 41.25) * mm, "end": v(4.75, 40) * mm});
            skLineSegment(sketch, "E247.MirrorCS", {"start": v(6, 40) * mm, "end": v(6, 37.5) * mm, "construction": true});
            skCircle(sketch, "E248", {"center": v(0, 30) * mm, "radius": 3.25 * mm});
            skLineSegment(sketch, "E249.bottom", {"start": v(-5, 23) * mm, "end": v(5, 23) * mm});
            skLineSegment(sketch, "E249.top", {"start": v(-5, 12) * mm, "end": v(5, 12) * mm});
            skLineSegment(sketch, "E249.left", {"start": v(-7, 21) * mm, "end": v(-7, 14) * mm});
            skLineSegment(sketch, "E249.right", {"start": v(7, 21) * mm, "end": v(7, 14) * mm});
            skPoint(sketch, "E250.visualSharp", {"position": v(-7, 23) * mm});
            skArc(sketch, "E250.filletArc", {"start": v(-5, 23) * mm, "mid": v(-6.41, 22.41) * mm, "end": v(-7, 21) * mm});
            skPoint(sketch, "E251.visualSharp", {"position": v(-7, 12) * mm});
            skArc(sketch, "E251.filletArc", {"start": v(-7, 14) * mm, "mid": v(-6.41, 12.59) * mm, "end": v(-5, 12) * mm});
            skPoint(sketch, "E252.visualSharp", {"position": v(7, 12) * mm});
            skArc(sketch, "E252.filletArc", {"start": v(5, 12) * mm, "mid": v(6.41, 12.59) * mm, "end": v(7, 14) * mm});
            skPoint(sketch, "E253.visualSharp", {"position": v(7, 23) * mm});
            skArc(sketch, "E253.filletArc", {"start": v(7, 21) * mm, "mid": v(6.41, 22.41) * mm, "end": v(5, 23) * mm});
            skLineSegment(sketch, "E254", {"start": v(-12, 18.75) * mm, "end": v(-12, 16.25) * mm, "construction": true});
            skLineSegment(sketch, "E255", {"start": v(-12, 1.25) * mm, "end": v(-12, -1.25) * mm, "construction": true});
            skArc(sketch, "E256.0.startCap", {"start": v(-13.25, 18.75) * mm, "mid": v(-12, 20) * mm, "end": v(-10.75, 18.75) * mm});
            skArc(sketch, "E256.0.endCap", {"start": v(-10.75, 16.25) * mm, "mid": v(-12, 15) * mm, "end": v(-13.25, 16.25) * mm});
            skLineSegment(sketch, "E256.0.left", {"start": v(-10.75, 18.75) * mm, "end": v(-10.75, 16.25) * mm});
            skLineSegment(sketch, "E256.0.right", {"start": v(-13.25, 18.75) * mm, "end": v(-13.25, 16.25) * mm});
            skArc(sketch, "E256.1.startCap", {"start": v(-13.25, 1.25) * mm, "mid": v(-12, 2.5) * mm, "end": v(-10.75, 1.25) * mm});
            skArc(sketch, "E256.1.endCap", {"start": v(-10.75, -1.25) * mm, "mid": v(-12, -2.5) * mm, "end": v(-13.25, -1.25) * mm});
            skLineSegment(sketch, "E256.1.left", {"start": v(-10.75, 1.25) * mm, "end": v(-10.75, -1.25) * mm});
            skLineSegment(sketch, "E256.1.right", {"start": v(-13.25, 1.25) * mm, "end": v(-13.25, -1.25) * mm});
            skLineSegment(sketch, "E257.MirrorCS", {"start": v(12, 18.75) * mm, "end": v(12, 16.25) * mm, "construction": true});
            skArc(sketch, "E258.MirrorCS", {"start": v(10.75, 16.25) * mm, "mid": v(12, 15) * mm, "end": v(13.25, 16.25) * mm});
            skArc(sketch, "E259.MirrorCS", {"start": v(13.25, 1.25) * mm, "mid": v(12, 2.5) * mm, "end": v(10.75, 1.25) * mm});
            skArc(sketch, "E260.MirrorCS", {"start": v(10.75, -1.25) * mm, "mid": v(12, -2.5) * mm, "end": v(13.25, -1.25) * mm});
            skLineSegment(sketch, "E261.MirrorCS", {"start": v(13.25, 1.25) * mm, "end": v(13.25, -1.25) * mm});
            skLineSegment(sketch, "E262.MirrorCS", {"start": v(13.25, 18.75) * mm, "end": v(13.25, 16.25) * mm});
            skLineSegment(sketch, "E263.MirrorCS", {"start": v(10.75, 1.25) * mm, "end": v(10.75, -1.25) * mm});
            skArc(sketch, "E264.MirrorCS", {"start": v(13.25, 18.75) * mm, "mid": v(12, 20) * mm, "end": v(10.75, 18.75) * mm});
            skLineSegment(sketch, "E265.MirrorCS", {"start": v(12, 1.25) * mm, "end": v(12, -1.25) * mm, "construction": true});
            skLineSegment(sketch, "E266.MirrorCS", {"start": v(10.75, 18.75) * mm, "end": v(10.75, 16.25) * mm});
            skLineSegment(sketch, "E267.bottom", {"start": v(-5, 5) * mm, "end": v(5, 5) * mm});
            skLineSegment(sketch, "E267.top", {"start": v(-5, -5) * mm, "end": v(5, -5) * mm});
            skLineSegment(sketch, "E267.left", {"start": v(-7, 3) * mm, "end": v(-7, -3) * mm});
            skLineSegment(sketch, "E267.right", {"start": v(7, 3) * mm, "end": v(7, -3) * mm});
            skPoint(sketch, "E268.visualSharp", {"position": v(-7, 0) * mm});
            skArc(sketch, "E268.filletArc", {"start": v(-5, 5) * mm, "mid": v(-6.41, 4.41) * mm, "end": v(-7, 3) * mm});
            skPoint(sketch, "E269.visualSharp", {"position": v(-7, -5) * mm});
            skArc(sketch, "E269.filletArc", {"start": v(-7, -3) * mm, "mid": v(-6.41, -4.41) * mm, "end": v(-5, -5) * mm});
            skPoint(sketch, "E270.visualSharp", {"position": v(7, -5) * mm});
            skArc(sketch, "E270.filletArc", {"start": v(5, -5) * mm, "mid": v(6.41, -4.41) * mm, "end": v(7, -3) * mm});
            skPoint(sketch, "E271.visualSharp", {"position": v(7, 5) * mm});
            skArc(sketch, "E271.filletArc", {"start": v(7, 3) * mm, "mid": v(6.41, 4.41) * mm, "end": v(5, 5) * mm});
            skArc(sketch, "E272", {"start": v(-8.2, -10.12) * mm, "mid": v(-10.84, -9.18) * mm, "end": v(-11.83, -11.8) * mm});
            skArc(sketch, "E273", {"start": v(-11.83, -14.2) * mm, "mid": v(-10.84, -16.82) * mm, "end": v(-8.2, -15.88) * mm});
            skArc(sketch, "E274", {"start": v(-6.59, -14.4) * mm, "mid": v(-5.63, -13) * mm, "end": v(-6.59, -11.6) * mm});
            skPoint(sketch, "E275.visualSharp", {"position": v(-8.36, -12.14) * mm});
            skArc(sketch, "E275.filletArc", {"start": v(-8.2, -10.12) * mm, "mid": v(-7.54, -11.01) * mm, "end": v(-6.59, -11.6) * mm});
            skPoint(sketch, "E276.visualSharp", {"position": v(-8.36, -13.86) * mm});
            skArc(sketch, "E276.filletArc", {"start": v(-6.59, -14.4) * mm, "mid": v(-7.54, -14.99) * mm, "end": v(-8.2, -15.88) * mm});
            skPoint(sketch, "E277.visualSharp", {"position": v(-10, -13) * mm});
            skArc(sketch, "E277.filletArc", {"start": v(-11.83, -14.2) * mm, "mid": v(-11.58, -13) * mm, "end": v(-11.83, -11.8) * mm});
            skPoint(sketch, "E278.MirrorP", {"position": v(8.36, -13.86) * mm});
            skArc(sketch, "E279.MirrorCS", {"start": v(8.2, -10.12) * mm, "mid": v(10.84, -9.18) * mm, "end": v(11.83, -11.8) * mm});
            skPoint(sketch, "E280.MirrorP", {"position": v(10, -13) * mm});
            skArc(sketch, "E281.MirrorCS", {"start": v(11.83, -14.2) * mm, "mid": v(10.84, -16.82) * mm, "end": v(8.2, -15.88) * mm});
            skArc(sketch, "E282.MirrorCS", {"start": v(11.83, -14.2) * mm, "mid": v(11.58, -13) * mm, "end": v(11.83, -11.8) * mm});
            skArc(sketch, "E283.MirrorCS", {"start": v(6.59, -14.4) * mm, "mid": v(7.54, -14.99) * mm, "end": v(8.2, -15.88) * mm});
            skArc(sketch, "E284.MirrorCS", {"start": v(8.2, -10.12) * mm, "mid": v(7.54, -11.01) * mm, "end": v(6.59, -11.6) * mm});
            skPoint(sketch, "E285.MirrorP", {"position": v(8.36, -12.14) * mm});
            skArc(sketch, "E286.MirrorCS", {"start": v(6.59, -14.4) * mm, "mid": v(5.63, -13) * mm, "end": v(6.59, -11.6) * mm});
            skSolve(sketch);
        }
        {
            var Q0;
            Q0 = qSketchRegion(id + "F20", true);
            extrude(context, id + "F21", {"entities" : qUnion([Q0]), "operationType" : NewBodyOperationType.REMOVE, "oppositeDirection" : true, "depth" : 25 * mm});
        }
        {
            var Q0;
            Q0=makeQuery(id+"F3.opExtrude","CAP_FACE",FACE,{"disambiguationData":[OSD([sQuery(id+"F2.wireOp",EDGE,"E42"),sQuery(id+"F2.wireOp",EDGE,"E43"),sQuery(id+"F2.wireOp",EDGE,"E44"),sQuery(id+"F2.wireOp",EDGE,"E45"),sQuery(id+"F2.wireOp",EDGE,"E46"),sQuery(id+"F2.wireOp",EDGE,"E48"),sQuery(id+"F2.wireOp",EDGE,"E49.filletArc"),sQuery(id+"F2.wireOp",EDGE,"E50.filletArc"),sQuery(id+"F2.wireOp",EDGE,"E51"),sQuery(id+"F2.wireOp",EDGE,"E52"),sQuery(id+"F2.wireOp",EDGE,"E54"),sQuery(id+"F2.wireOp",EDGE,"E55.MirrorCS"),sQuery(id+"F2.wireOp",EDGE,"E56.MirrorCS"),sQuery(id+"F2.wireOp",EDGE,"E58.MirrorCS"),sQuery(id+"F2.wireOp",EDGE,"E59.MirrorCS"),sQuery(id+"F2.wireOp",EDGE,"E60.MirrorC"),sQuery(id+"F2.wireOp",EDGE,"E61.MirrorC"),sQuery(id+"F2.wireOp",EDGE,"E62.MirrorC"),sQuery(id+"F2.wireOp",EDGE,"E63.MirrorCS"),sQuery(id+"F2.wireOp",EDGE,"E65.MirrorCS"),sQuery(id+"F2.wireOp",EDGE,"E67.MirrorCS"),sQuery(id+"F2.wireOp",EDGE,"E68.MirrorCS"),sQuery(id+"F2.wireOp",EDGE,"E72.MirrorCS"),sQuery(id+"F2.wireOp",EDGE,"E73.MirrorCS"),sQuery(id+"F2.wireOp",EDGE,"E74.MirrorCS"),sQuery(id+"F2.wireOp",EDGE,"E75.MirrorCS"),sQuery(id+"F2.wireOp",EDGE,"E76.MirrorCS"),sQuery(id+"F2.wireOp",EDGE,"E77.MirrorCS"),sQuery(id+"F2.wireOp",EDGE,"E78.MirrorCS"),sQuery(id+"F2.wireOp",EDGE,"E79.MirrorCS"),sQuery(id+"F2.wireOp",EDGE,"E83.MirrorC"),sQuery(id+"F2.wireOp",EDGE,"E84.MirrorC"),sQuery(id+"F2.wireOp",EDGE,"E85.MirrorCS"),sQuery(id+"F2.wireOp",EDGE,"E86.MirrorC"),sQuery(id+"F2.wireOp",EDGE,"E87.MirrorC"),sQuery(id+"F2.wireOp",EDGE,"E88.MirrorC"),sQuery(id+"F2.wireOp",EDGE,"E89.MirrorC"),sQuery(id+"F2.wireOp",EDGE,"E90.MirrorCS"),sQuery(id+"F2.wireOp",EDGE,"E91.MirrorCS"),sQuery(id+"F2.wireOp",EDGE,"E92.MirrorCS"),sQuery(id+"F2.wireOp",EDGE,"E93.MirrorCS"),sQuery(id+"F2.wireOp",EDGE,"E94.MirrorCS"),sQuery(id+"F2.wireOp",EDGE,"E95.MirrorCS"),sQuery(id+"F2.wireOp",EDGE,"E96.MirrorCS"),sQuery(id+"F2.wireOp",EDGE,"E97.bottom"),sQuery(id+"F2.wireOp",EDGE,"E97.top"),sQuery(id+"F2.wireOp",EDGE,"E97.left"),sQuery(id+"F2.wireOp",EDGE,"E97.right"),sQuery(id+"F2.wireOp",EDGE,"E98.MirrorCS"),sQuery(id+"F2.wireOp",EDGE,"E99.MirrorCS"),sQuery(id+"F2.wireOp",EDGE,"E100.MirrorCS"),sQuery(id+"F2.wireOp",EDGE,"E101.MirrorCS"),sQuery(id+"F2.wireOp",EDGE,"E104"),sQuery(id+"F2.wireOp",EDGE,"E105.filletArc"),sQuery(id+"F2.wireOp",EDGE,"E106.MirrorCS"),sQuery(id+"F2.wireOp",EDGE,"E107.MirrorCS"),sQuery(id+"F2.wireOp",EDGE,"E108.MirrorCS"),sQuery(id+"F2.wireOp",EDGE,"E109.MirrorCS"),sQuery(id+"F2.wireOp",EDGE,"E110.MirrorCS"),sQuery(id+"F2.wireOp",EDGE,"E111.MirrorCS")])],"isStart":false});
            var sketch = newSketch(context, id + "F22", { "sketchPlane" : qUnion([Q0])});
            skCircle(sketch, "E287", {"center": v(27, -6) * mm, "radius": 3.25 * mm});
            skPoint(sketch, "E287.centerSnap0", {"position": v(17, 0) * mm});
            skArc(sketch, "E288", {"start": v(22, -9.75) * mm, "mid": v(33.25, -6) * mm, "end": v(22, -2.25) * mm});
            skLineSegment(sketch, "E289", {"start": v(22, -2.25) * mm, "end": v(22, -9.75) * mm});
            skSolve(sketch);
        }
        {
            var Q0;
            Q0 = qSketchRegion(id + "F22", true);
            extrude(context, id + "F23", {"entities" : qUnion([Q0]), "operationType" : NewBodyOperationType.ADD, "oppositeDirection" : true, "depth" : 1.5 * mm});
        }
        {
            var Q0;
            Q0=makeQuery(id+"F23.boolean.opBoolean","INTERSECT",EDGE,{"derivedFrom":[makeQuery(id+"F3.opExtrude","SWEPT_FACE",FACE,{"disambiguationData":[OSD([sQuery(id+"F2.wireOp",EDGE,"E108.MirrorCS")])]}),makeQuery(id+"F23.opExtrude","SWEPT_FACE",FACE,{"disambiguationData":[OSD([sQuery(id+"F22.wireOp",EDGE,"E288")])]})]});
            var Q1;
            Q1=makeQuery(id+"F23.boolean.opBoolean","INTERSECT",EDGE,{"derivedFrom":[makeQuery(id+"F3.opExtrude","SWEPT_FACE",FACE,{"disambiguationData":[OSD([sQuery(id+"F2.wireOp",EDGE,"E106.MirrorCS")])]}),makeQuery(id+"F23.opExtrude","SWEPT_FACE",FACE,{"disambiguationData":[OSD([sQuery(id+"F22.wireOp",EDGE,"E288")])]})]});
            fillet(context, id + "F24", {"entities" : qUnion([Q0, Q1]), "radius" : 4 * mm, "tangentPropagation" : true, "allowEdgeOverflow" : false});
        }
        {
            var Q0;
            Q0=makeQuery(id+"F7.opExtrude","SWEPT_EDGE",EDGE,{"disambiguationData":[OSD([sQuery(id+"F6.wireOp",EDGE,"E130"),sQuery(id+"F6.wireOp",EDGE,"E131")])]});
            fillet(context, id + "F25", {"entities" : qUnion([Q0]), "radius" : 3 * mm, "tangentPropagation" : true, "allowEdgeOverflow" : false});
        }
        {
            var Q0;
            Q0=qCreatedBy(makeId("Top.planeOp"),FACE);
            var sketch = newSketch(context, id + "F26", { "sketchPlane" : qUnion([Q0])});
            skCircle(sketch, "E290", {"center": v(0, 0) * mm, "radius": 2.23 * mm});
            skCircle(sketch, "E291", {"center": v(0, 0) * mm, "radius": 1.25 * mm});
            skSolve(sketch);
        }
        {
            var Q0;
            Q0=makeQuery(id+"F26.imprint","IMPRINT",FACE,{"disambiguationData":[TD([[makeQuery(id+"F26.imprint","IMPRINT",EDGE,{"derivedFrom":sQuery(id+"F26.wireOp",EDGE,"E290")}),1.0]])]});
            extrude(context, id + "F27", {"entities" : qUnion([Q0]), "depth" : 1.5 * mm});
        }
        {
            var Q0;
            Q0=makeQuery(id+"F27.opExtrude","CAP_FACE",FACE,{"disambiguationData":[OSD([sQuery(id+"F26.wireOp",EDGE,"E290"),sQuery(id+"F26.wireOp",EDGE,"E291")])],"isStart":false});
            var sketch = newSketch(context, id + "F28", { "sketchPlane" : qUnion([Q0])});
            skCircle(sketch, "E292", {"center": v(0, 0) * mm, "radius": 2.75 * mm});
            skCircle(sketch, "E293", {"center": v(0, 0) * mm, "radius": 1.25 * mm});
            skSolve(sketch);
        }
        {
            var Q0;
            Q0 = qSketchRegion(id + "F28", true);
            extrude(context, id + "F29", {"entities" : qUnion([Q0]), "operationType" : NewBodyOperationType.ADD, "depth" : 1.5 * mm});
        }
        {
            var Q0;
            Q0=makeQuery(id+"F15.opExtrude","SWEPT_EDGE",EDGE,{"disambiguationData":[OSD([sQuery(id+"F14.wireOp",EDGE,"E229"),sQuery(id+"F14.wireOp",EDGE,"E230.trimOffspring")])]});
            var Q1;
            Q1=makeQuery(id+"F15.opExtrude","SWEPT_EDGE",EDGE,{"disambiguationData":[OSD([sQuery(id+"F14.wireOp",EDGE,"E224"),sQuery(id+"F14.wireOp",EDGE,"E229")])]});
            fillet(context, id + "F30", {"entities" : qUnion([Q0, Q1]), "radius" : 3 * mm, "tangentPropagation" : true, "allowEdgeOverflow" : false});
        }
    });
